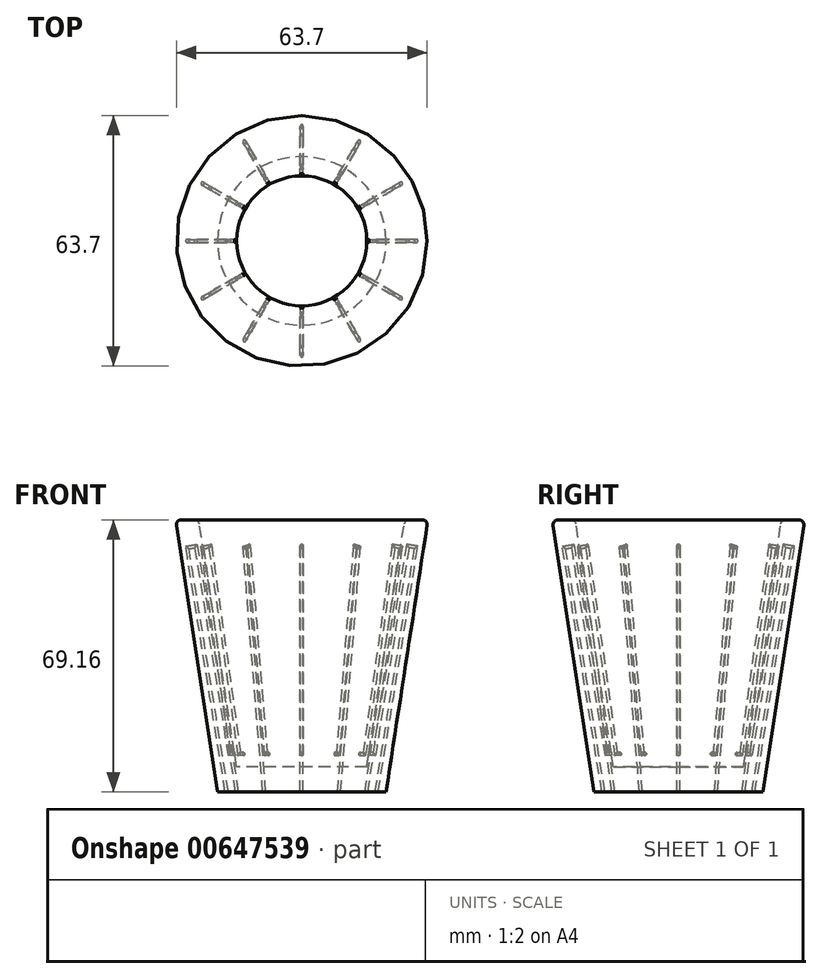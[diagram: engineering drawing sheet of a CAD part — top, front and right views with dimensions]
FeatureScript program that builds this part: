
annotation { "Feature Type Name" : "Feature", "Feature Type Description" : "" }
export const myFeature = defineFeature(function(context is Context, id is Id, definition is map)
    precondition{}
    {
        {
            var Q0;
            Q0=qCreatedBy(makeId("Front.planeOp"),FACE);
            var sketch = newSketch(context, id + "F0", { "sketchPlane" : qUnion([Q0])});
            skLineSegment(sketch, "E0", {"start": v(0, 7.92) * mm, "end": v(16.51, 7.92) * mm});
            skLineSegment(sketch, "E1", {"start": v(16.51, 7.92) * mm, "end": v(26.18, 70.68) * mm});
            skLineSegment(sketch, "E2", {"start": v(26.18, 70.68) * mm, "end": v(32.07, 70.68) * mm});
            skLineSegment(sketch, "E3", {"start": v(32.07, 70.68) * mm, "end": v(21.4, 1.52) * mm});
            skLineSegment(sketch, "E4", {"start": v(21.4, 1.52) * mm, "end": v(0, 1.52) * mm});
            skLineSegment(sketch, "E5", {"start": v(0, 1.52) * mm, "end": v(0, 7.92) * mm});
            skLineSegment(sketch, "E6", {"start": v(0, 7.92) * mm, "end": v(0, 72.76) * mm});
            skLineSegment(sketch, "E7", {"start": v(0, 72.76) * mm, "end": v(0, 7.92) * mm});
            skSolve(sketch);
        }
        {
            var Q0;
            Q0=makeQuery(id+"F0.imprint","IMPRINT",FACE,{"disambiguationData":[TD([[makeQuery(id+"F0.imprint","IMPRINT",EDGE,{"derivedFrom":sQuery(id+"F0.wireOp",EDGE,"E0")}),-1.0]])]});
            var Q1;
            Q1=sQuery(id+"F0.wireOp",EDGE,"E7");
            revolve(context, id + "F1", {"entities" : qUnion([Q0]), "axis" : qUnion([Q1]), "revolveType" : RevolveType.FULL});
        }
        {
            var Q0;
            Q0=makeQuery(id+"F1.opRevolve","SWEPT_EDGE",EDGE,{"disambiguationData":[OSD([sQuery(id+"F0.wireOp",EDGE,"E2"),sQuery(id+"F0.wireOp",EDGE,"E3")])]});
            var Q1;
            Q1=makeQuery(id+"F1.opRevolve","SWEPT_EDGE",EDGE,{"disambiguationData":[OSD([sQuery(id+"F0.wireOp",EDGE,"E1"),sQuery(id+"F0.wireOp",EDGE,"E2")])]});
            fillet(context, id + "F2", {"entities" : qUnion([Q0, Q1]), "radius" : 1.27 * mm, "tangentPropagation" : true, "allowEdgeOverflow" : false});
        }
        {
            var Q0;
            Q0=qCreatedBy(makeId("Front.planeOp"),FACE);
            var sketch = newSketch(context, id + "F3", { "sketchPlane" : qUnion([Q0])});
            skLineSegment(sketch, "E8", {"start": v(16.03, 11.2) * mm, "end": v(18.38, 11.2) * mm});
            skLineSegment(sketch, "E9", {"start": v(18.38, 11.2) * mm, "end": v(26.9, 63.99) * mm});
            skLineSegment(sketch, "E10", {"start": v(26.9, 63.99) * mm, "end": v(29.07, 63.64) * mm});
            skLineSegment(sketch, "E11", {"start": v(29.07, 63.64) * mm, "end": v(18.8, 0) * mm});
            skSolve(sketch);
        }
        {
            var Q0;
            Q0=qCreatedBy(makeId("Top.planeOp"),FACE);
            var sketch = newSketch(context, id + "F4", { "sketchPlane" : qUnion([Q0])});
            skCircle(sketch, "E12", {"center": v(18.8, 0) * mm, "radius": 0.38 * mm});
            skSolve(sketch);
        }
        {
            var Q0;
            Q0=makeQuery(id+"F4.imprint","IMPRINT",FACE,{"disambiguationData":[TD([[makeQuery(id+"F4.imprint","IMPRINT",EDGE,{"derivedFrom":sQuery(id+"F4.wireOp",EDGE,"E12")}),1.0]])]});
            var Q1;
            Q1=sQuery(id+"F3.wireOp",EDGE,"E11");
            var Q2;
            Q2=sQuery(id+"F3.wireOp",EDGE,"E8");
            var Q3;
            Q3=sQuery(id+"F3.wireOp",EDGE,"E9");
            var Q4;
            Q4=sQuery(id+"F3.wireOp",EDGE,"E10");
            sweep(context, id + "F5", {"profiles" : qUnion([Q0]), "path" : qUnion([Q1, Q2, Q3, Q4])});
        }
        {
            var Q0;
            Q0=makeQuery(id+"F5.opSweep","SWEPT_BODY",BODY,{"disambiguationData":[OSD([sQuery(id+"F3.wireOp",EDGE,"E11"),sQuery(id+"F4.wireOp",EDGE,"E12")])]});
            var Q1;
            Q1=sQuery(id+"F0.wireOp",EDGE,"E7");
            circularPattern(context, id + "F6", {"entities" : qUnion([Q0]), "axis" : qUnion([Q1]), "angle" : 360 * degree, "instanceCount" : 12, "oppositeDirection" : true, "equalSpace" : true});
        }
        {
            var Q0;
            Q0=makeQuery(id+"F6.opPattern","COPY",BODY,{"derivedFrom":makeQuery(id+"F5.opSweep","SWEPT_BODY",BODY,{"disambiguationData":[OSD([sQuery(id+"F3.wireOp",EDGE,"E11"),sQuery(id+"F4.wireOp",EDGE,"E12")])]}),"instanceName":"7"});
            var Q1;
            Q1=makeQuery(id+"F6.opPattern","COPY",BODY,{"derivedFrom":makeQuery(id+"F5.opSweep","SWEPT_BODY",BODY,{"disambiguationData":[OSD([sQuery(id+"F3.wireOp",EDGE,"E11"),sQuery(id+"F4.wireOp",EDGE,"E12")])]}),"instanceName":"6"});
            var Q2;
            Q2=makeQuery(id+"F6.opPattern","COPY",BODY,{"derivedFrom":makeQuery(id+"F5.opSweep","SWEPT_BODY",BODY,{"disambiguationData":[OSD([sQuery(id+"F3.wireOp",EDGE,"E11"),sQuery(id+"F4.wireOp",EDGE,"E12")])]}),"instanceName":"5"});
            var Q3;
            Q3=makeQuery(id+"F6.opPattern","COPY",BODY,{"derivedFrom":makeQuery(id+"F5.opSweep","SWEPT_BODY",BODY,{"disambiguationData":[OSD([sQuery(id+"F3.wireOp",EDGE,"E11"),sQuery(id+"F4.wireOp",EDGE,"E12")])]}),"instanceName":"8"});
            var Q4;
            Q4=makeQuery(id+"F6.opPattern","COPY",BODY,{"derivedFrom":makeQuery(id+"F5.opSweep","SWEPT_BODY",BODY,{"disambiguationData":[OSD([sQuery(id+"F3.wireOp",EDGE,"E11"),sQuery(id+"F4.wireOp",EDGE,"E12")])]}),"instanceName":"4"});
            var Q5;
            Q5=makeQuery(id+"F6.opPattern","COPY",BODY,{"derivedFrom":makeQuery(id+"F5.opSweep","SWEPT_BODY",BODY,{"disambiguationData":[OSD([sQuery(id+"F3.wireOp",EDGE,"E11"),sQuery(id+"F4.wireOp",EDGE,"E12")])]}),"instanceName":"9"});
            var Q6;
            Q6=makeQuery(id+"F6.opPattern","COPY",BODY,{"derivedFrom":makeQuery(id+"F5.opSweep","SWEPT_BODY",BODY,{"disambiguationData":[OSD([sQuery(id+"F3.wireOp",EDGE,"E11"),sQuery(id+"F4.wireOp",EDGE,"E12")])]}),"instanceName":"10"});
            var Q7;
            Q7=makeQuery(id+"F6.opPattern","COPY",BODY,{"derivedFrom":makeQuery(id+"F5.opSweep","SWEPT_BODY",BODY,{"disambiguationData":[OSD([sQuery(id+"F3.wireOp",EDGE,"E11"),sQuery(id+"F4.wireOp",EDGE,"E12")])]}),"instanceName":"3"});
            var Q8;
            Q8=makeQuery(id+"F5.opSweep","SWEPT_BODY",BODY,{"disambiguationData":[OSD([sQuery(id+"F3.wireOp",EDGE,"E11"),sQuery(id+"F4.wireOp",EDGE,"E12")])]});
            var Q9;
            Q9=makeQuery(id+"F6.opPattern","COPY",BODY,{"derivedFrom":makeQuery(id+"F5.opSweep","SWEPT_BODY",BODY,{"disambiguationData":[OSD([sQuery(id+"F3.wireOp",EDGE,"E11"),sQuery(id+"F4.wireOp",EDGE,"E12")])]}),"instanceName":"1"});
            var Q10;
            Q10=makeQuery(id+"F6.opPattern","COPY",BODY,{"derivedFrom":makeQuery(id+"F5.opSweep","SWEPT_BODY",BODY,{"disambiguationData":[OSD([sQuery(id+"F3.wireOp",EDGE,"E11"),sQuery(id+"F4.wireOp",EDGE,"E12")])]}),"instanceName":"11"});
            var Q11;
            Q11=makeQuery(id+"F6.opPattern","COPY",BODY,{"derivedFrom":makeQuery(id+"F5.opSweep","SWEPT_BODY",BODY,{"disambiguationData":[OSD([sQuery(id+"F3.wireOp",EDGE,"E11"),sQuery(id+"F4.wireOp",EDGE,"E12")])]}),"instanceName":"2"});
            var Q12;
            Q12=makeQuery(id+"F1.opRevolve","SWEPT_BODY",BODY,{"disambiguationData":[OSD([sQuery(id+"F0.wireOp",EDGE,"E0"),sQuery(id+"F0.wireOp",EDGE,"E1"),sQuery(id+"F0.wireOp",EDGE,"E2"),sQuery(id+"F0.wireOp",EDGE,"E3"),sQuery(id+"F0.wireOp",EDGE,"E4"),sQuery(id+"F0.wireOp",EDGE,"E5")])]});
            booleanBodies(context, id + "F7", {"operationType" : BooleanOperationType.SUBTRACTION, "tools" : qUnion([Q0, Q1, Q2, Q3, Q4, Q5, Q6, Q7, Q8, Q9, Q10, Q11]), "targets" : qUnion([Q12])});
        }
    });
